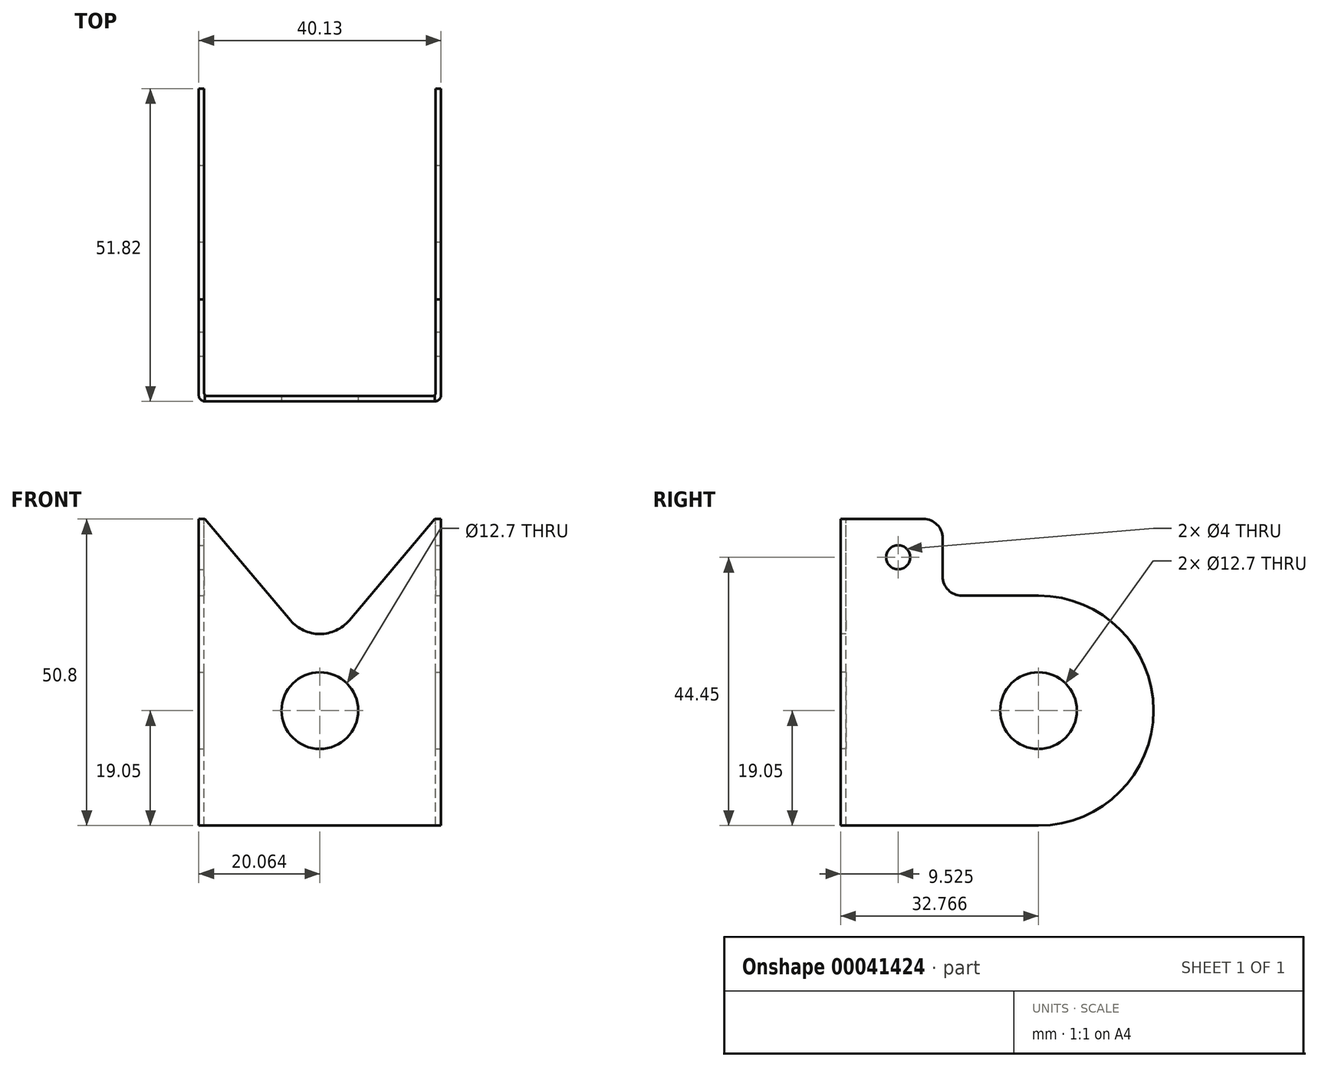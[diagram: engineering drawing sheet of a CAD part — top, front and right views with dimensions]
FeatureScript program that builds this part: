
annotation { "Feature Type Name" : "Feature", "Feature Type Description" : "" }
export const myFeature = defineFeature(function(context is Context, id is Id, definition is map)
    precondition{}
    {
        {
            var Q0;
            Q0=qCreatedBy(makeId("Top.planeOp"),FACE);
            var sketch = newSketch(context, id + "F0", { "sketchPlane" : qUnion([Q0])});
            skLineSegment(sketch, "E0.bottom", {"start": v(-1.02, 0) * mm, "end": v(-39.12, 0) * mm});
            skLineSegment(sketch, "E0.left", {"start": v(0, 1.02) * mm, "end": v(0, 51.82) * mm});
            skLineSegment(sketch, "E0.right", {"start": v(-40.13, 1.02) * mm, "end": v(-40.13, 51.82) * mm});
            skPoint(sketch, "E1.visualSharp", {"position": v(-40.13, 0) * mm});
            skArc(sketch, "E1.filletArc", {"start": v(-40.13, 1.02) * mm, "mid": v(-39.83, 0.3) * mm, "end": v(-39.12, 0) * mm});
            skPoint(sketch, "E2.visualSharp", {"position": v(0, 0) * mm});
            skArc(sketch, "E2.filletArc", {"start": v(-1.02, 0) * mm, "mid": v(-0.3, 0.3) * mm, "end": v(0, 1.02) * mm});
            skLineSegment(sketch, "E3.0", {"start": v(-0.89, 1.4) * mm, "end": v(-0.89, 51.82) * mm});
            skLineSegment(sketch, "E3.1", {"start": v(-1.4, 0.89) * mm, "end": v(-38.73, 0.89) * mm});
            skLineSegment(sketch, "E3.2", {"start": v(-39.24, 1.4) * mm, "end": v(-39.24, 51.82) * mm});
            skLineSegment(sketch, "E4", {"start": v(-39.24, 51.82) * mm, "end": v(-40.13, 51.82) * mm});
            skLineSegment(sketch, "E5", {"start": v(-0.89, 51.82) * mm, "end": v(0, 51.82) * mm});
            skPoint(sketch, "E6.visualSharp", {"position": v(-39.24, 0.89) * mm});
            skArc(sketch, "E6.filletArc", {"start": v(-39.24, 1.4) * mm, "mid": v(-39.1, 1.04) * mm, "end": v(-38.73, 0.89) * mm});
            skPoint(sketch, "E7.visualSharp", {"position": v(-0.89, 0.89) * mm});
            skArc(sketch, "E7.filletArc", {"start": v(-1.4, 0.89) * mm, "mid": v(-1.04, 1.04) * mm, "end": v(-0.89, 1.4) * mm});
            skSolve(sketch);
        }
        {
            var Q0;
            Q0 = qSketchRegion(id + "F0", true);
            extrude(context, id + "F1", {"entities" : qUnion([Q0]), "oppositeDirection" : true, "depth" : 50.8 * mm});
        }
        {
            var Q0;
            Q0=makeQuery(id+"F1.opExtrude","SWEPT_FACE",FACE,{"disambiguationData":[OSD([sQuery(id+"F0.wireOp",EDGE,"E0.bottom")])]});
            var sketch = newSketch(context, id + "F2", { "sketchPlane" : qUnion([Q0])});
            skCircle(sketch, "E8", {"center": v(-20.07, -31.75) * mm, "radius": 6.35 * mm});
            skLineSegment(sketch, "E9", {"start": v(-0.67, -31.75) * mm, "end": v(-39.12, -31.75) * mm, "construction": true});
            skLineSegment(sketch, "E10", {"start": v(-20.07, 0) * mm, "end": v(-20.07, -50.8) * mm, "construction": true});
            skArc(sketch, "E11", {"start": v(-24.92, -16.8) * mm, "mid": v(-20.07, -19.05) * mm, "end": v(-15.22, -16.8) * mm});
            skLineSegment(sketch, "E12", {"start": v(-39.12, 0) * mm, "end": v(-24.92, -16.8) * mm});
            skLineSegment(sketch, "E13", {"start": v(-1.02, 0) * mm, "end": v(-15.22, -16.8) * mm});
            skSolve(sketch);
        }
        {
            var Q0;
            Q0 = qSketchRegion(id + "F2", true);
            var Q1;
            Q1=makeQuery(id+"F2.imprint","IMPRINT",FACE,{"disambiguationData":[TD([[makeQuery(id+"F2.imprint","IMPRINT",EDGE,{"derivedFrom":sQuery(id+"F2.wireOp",EDGE,"E11")}),1.0]])]});
            extrude(context, id + "F3", {"entities" : qUnion([Q0, Q1]), "operationType" : NewBodyOperationType.REMOVE, "oppositeDirection" : true, "depth" : 25.4 * mm});
        }
        {
            var Q0;
            Q0=makeQuery(id+"F1.opExtrude","SWEPT_FACE",FACE,{"disambiguationData":[OSD([sQuery(id+"F0.wireOp",EDGE,"E0.left")])]});
            var sketch = newSketch(context, id + "F4", { "sketchPlane" : qUnion([Q0])});
            skArc(sketch, "E14", {"start": v(32.77, -50.8) * mm, "mid": v(51.82, -31.75) * mm, "end": v(32.77, -12.7) * mm});
            skCircle(sketch, "E15", {"center": v(32.77, -31.75) * mm, "radius": 6.35 * mm});
            skLineSegment(sketch, "E16", {"start": v(32.77, -50.8) * mm, "end": v(32.77, 0) * mm, "construction": true});
            skLineSegment(sketch, "E17", {"start": v(1.02, 0) * mm, "end": v(1.02, -50.8) * mm});
            skLineSegment(sketch, "E18", {"start": v(1.02, -50.8) * mm, "end": v(32.77, -50.8) * mm});
            skLineSegment(sketch, "E19", {"start": v(32.77, -12.7) * mm, "end": v(20.07, -12.7) * mm});
            skLineSegment(sketch, "E20", {"start": v(16.9, -9.52) * mm, "end": v(16.9, -3.18) * mm});
            skLineSegment(sketch, "E21", {"start": v(13.72, 0) * mm, "end": v(1.02, 0) * mm});
            skPoint(sketch, "E22.visualSharp", {"position": v(16.9, -12.7) * mm});
            skArc(sketch, "E22.filletArc", {"start": v(16.9, -9.52) * mm, "mid": v(17.82, -11.77) * mm, "end": v(20.07, -12.7) * mm});
            skPoint(sketch, "E23.visualSharp", {"position": v(16.9, 0) * mm});
            skArc(sketch, "E23.filletArc", {"start": v(16.9, -3.18) * mm, "mid": v(15.96, -0.93) * mm, "end": v(13.72, 0) * mm});
            skCircle(sketch, "E24", {"center": v(9.53, -6.35) * mm, "radius": 2 * mm});
            skSolve(sketch);
        }
        {
            var Q0;
            {var subQ0=sQuery(id+"F0.wireOp",EDGE,"E0.left");var subQ1=makeQuery(id+"F1.opExtrude","CAP_EDGE",EDGE,{"disambiguationData":[OSD([subQ0])],"isStart":false});var subQ2=sQuery(id+"F4.wireOp",EDGE,"E14");var subQ3=makeQuery(id+"F4.imprint","INTERSECT",VERTEX,{"derivedFrom":[subQ1,subQ2]});Q0=makeQuery(id+"F4.imprint","IMPRINT",FACE,{"disambiguationData":[TD([[makeQuery(id+"F4.imprint","IMPRINT",EDGE,{"disambiguationData":[TD([[subQ3,-1.0]])],"derivedFrom":subQ2}),-1.0]])]});}
            var Q1;
            {var subQ0=sQuery(id+"F0.wireOp",EDGE,"E0.left");var subQ2=sQuery(id+"F4.wireOp",EDGE,"E14");var subQ4=makeQuery(id+"F1.opExtrude","CAP_EDGE",EDGE,{"disambiguationData":[OSD([subQ0])],"isStart":true});var subQ6=makeQuery(id+"F4.imprint","INTERSECT",VERTEX,{"derivedFrom":[subQ4,subQ2]});Q1=makeQuery(id+"F4.imprint","IMPRINT",FACE,{"disambiguationData":[TD([[makeQuery(id+"F4.imprint","IMPRINT",EDGE,{"disambiguationData":[TD([[subQ6,1.0]])],"derivedFrom":subQ2}),-1.0]])]});}
            var Q2;
            Q2=makeQuery(id+"F4.imprint","IMPRINT",FACE,{"disambiguationData":[TD([[makeQuery(id+"F4.imprint","IMPRINT",EDGE,{"derivedFrom":sQuery(id+"F4.wireOp",EDGE,"E15")}),1.0]])]});
            var Q3;
            {var subQ7=sQuery(id+"F4.wireOp",EDGE,"E19");Q3=makeQuery(id+"F4.imprint","IMPRINT",FACE,{"disambiguationData":[TD([[makeQuery(id+"F4.imprint","IMPRINT",EDGE,{"derivedFrom":subQ7}),-1.0]])]});}
            var Q4;
            Q4=makeQuery(id+"F4.imprint","IMPRINT",FACE,{"disambiguationData":[TD([[makeQuery(id+"F4.imprint","IMPRINT",EDGE,{"derivedFrom":sQuery(id+"F4.wireOp",EDGE,"E24")}),1.0]])]});
            extrude(context, id + "F5", {"entities" : qUnion([Q0, Q1, Q2, Q3, Q4]), "operationType" : NewBodyOperationType.REMOVE, "endBound" : BoundingType.THROUGH_ALL, "oppositeDirection" : true, "depth" : 25.4 * mm});
        }
    });
